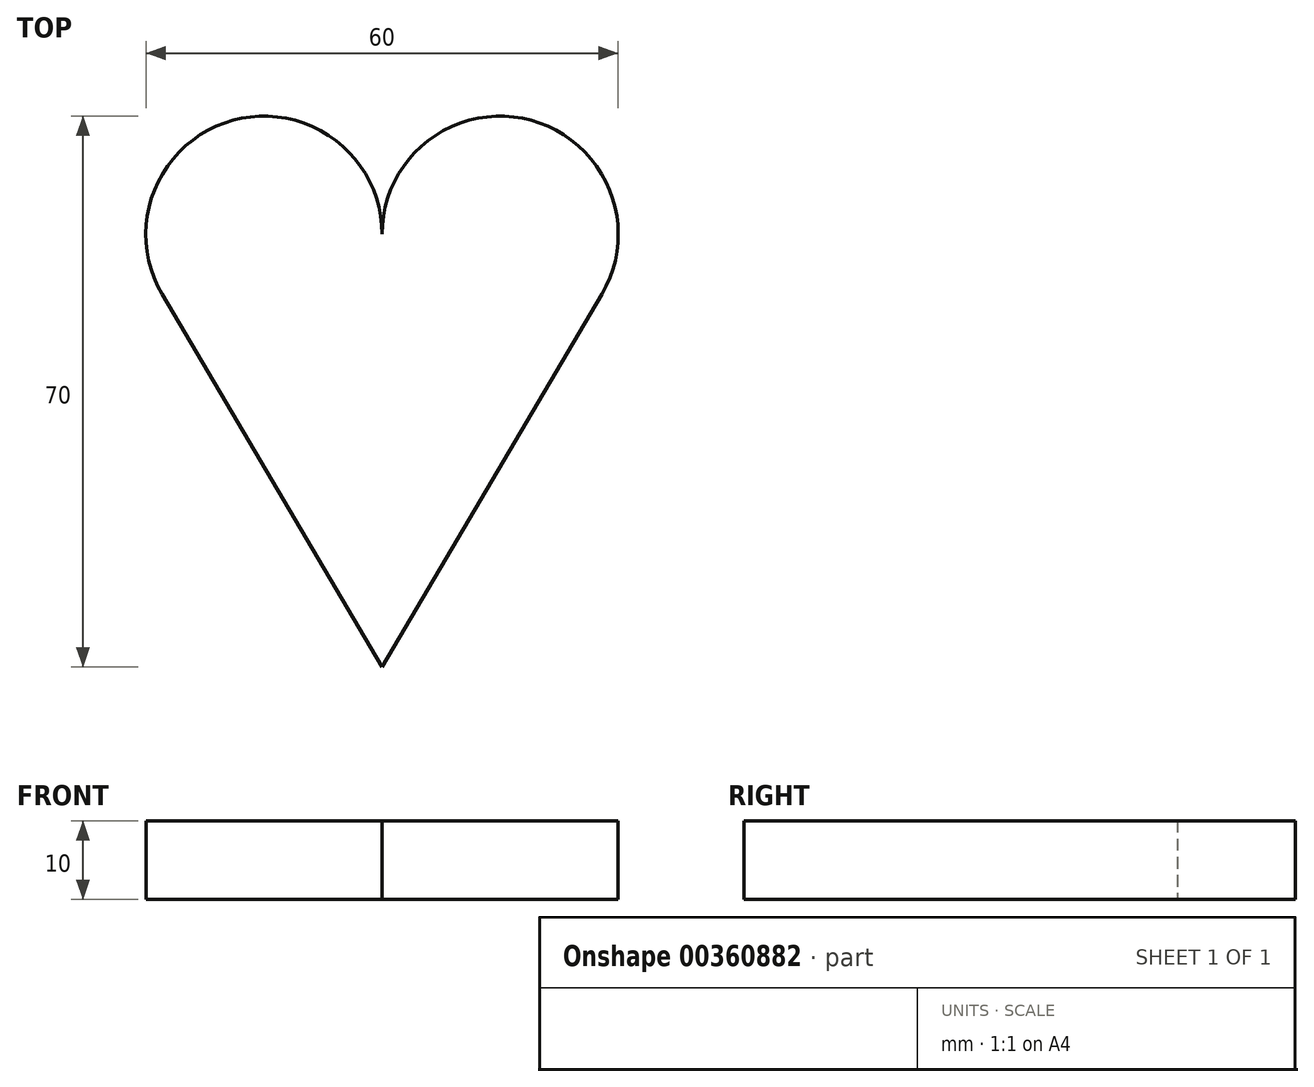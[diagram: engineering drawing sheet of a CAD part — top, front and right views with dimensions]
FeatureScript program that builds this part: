
annotation { "Feature Type Name" : "Feature", "Feature Type Description" : "" }
export const myFeature = defineFeature(function(context is Context, id is Id, definition is map)
    precondition{}
    {
        {
            var Q0;
            Q0=qCreatedBy(makeId("Top.planeOp"),FACE);
            var sketch = newSketch(context, id + "F0", { "sketchPlane" : qUnion([Q0])});
            skCircle(sketch, "E0", {"center": v(-28.87, 34.05) * mm, "radius": 15 * mm});
            skCircle(sketch, "E1", {"center": v(1.13, 34.05) * mm, "radius": 15 * mm});
            skPoint(sketch, "E1.first.point", {"position": v(-13.87, 34.05) * mm});
            skPoint(sketch, "E1.second.point", {"position": v(16.07, 32.8) * mm});
            skPoint(sketch, "E1.third.point", {"position": v(14.9, 28.12) * mm});
            skLineSegment(sketch, "E2", {"start": v(-41.8, 26.43) * mm, "end": v(-13.87, -20.95) * mm});
            skLineSegment(sketch, "E3", {"start": v(-13.87, -20.95) * mm, "end": v(14.05, 26.43) * mm});
            skSolve(sketch);
        }
        {
            var Q0;
            Q0 = qSketchRegion(id + "F0", true);
            extrude(context, id + "F1", {"entities" : qUnion([Q0]), "depth" : 10 * mm});
        }
    });
